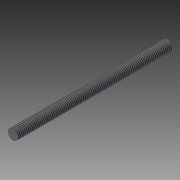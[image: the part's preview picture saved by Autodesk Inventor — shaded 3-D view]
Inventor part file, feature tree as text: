
AUTODESK INVENTOR PART (.ipt)
format: ipt  version: 2015 (Build 190159000, 159)  size: 74,240 bytes
history: native  units: in
note: dims shown in document units (in); Inventor stores cm internally (conversion verified against a paired STEP export)
features: plane x1, extrude x1, thread x1, sketch x1
ambient origin geometry x8: Origin, YZ Plane, XZ Plane, XY Plane, X Axis, Y Axis, Z Axis, Center Point
bodies: Solid1 (feature_tree)
feature tree (4):
  plane  "Work Plane1"
  extrude  "Extrusion1"  Depth=0.3937in TaperAngle=0.0deg
  thread  "Thread1"  [1 undecoded]
  sketch  "Sketch1"  dims[d0=0.1181in d1=1.5748in d2=0.1969in d3=0.0in d4=0.0in d5=0.3937in d6=0.0in]
note: 1 required parameter value undecoded (feature->parameter linkage not recoverable at this tier; creation-order binding heuristic only, values carry confidence <= 0.55)
